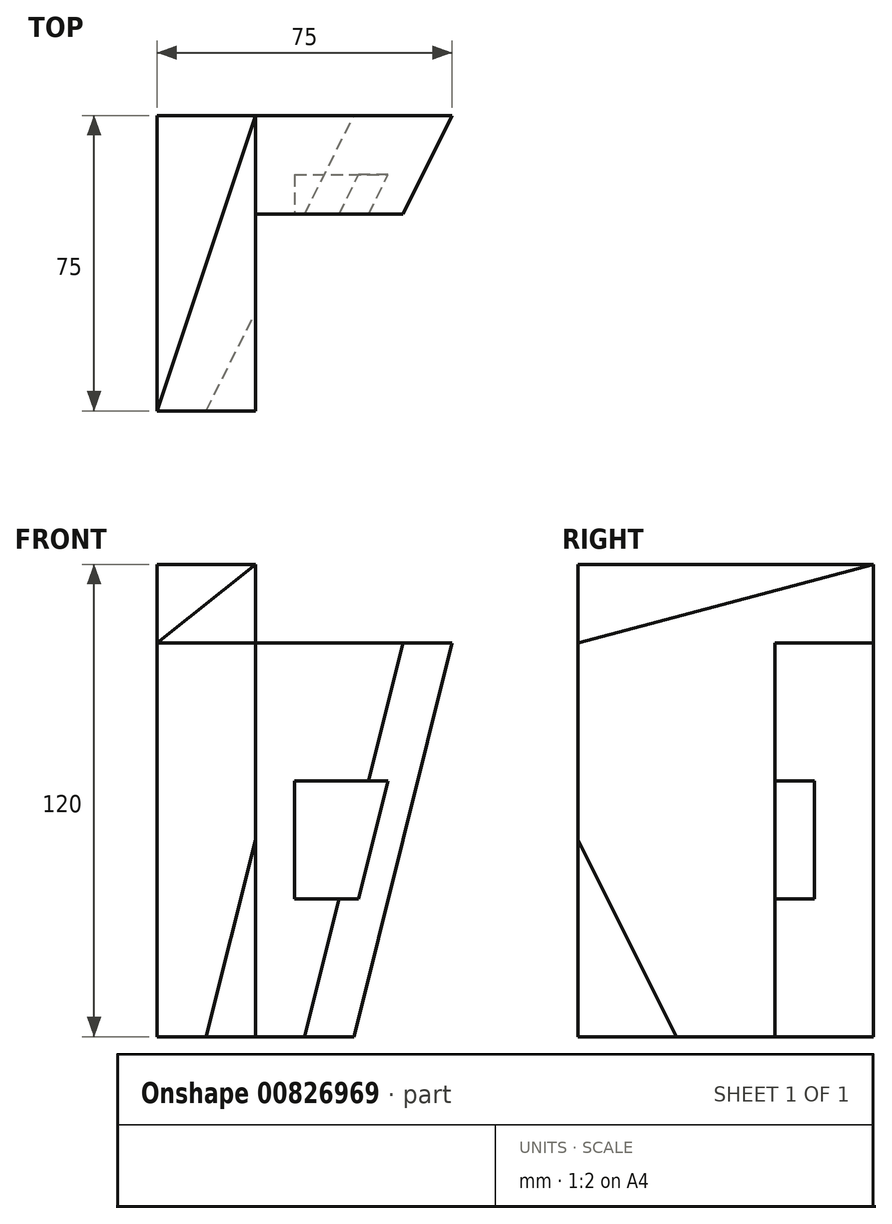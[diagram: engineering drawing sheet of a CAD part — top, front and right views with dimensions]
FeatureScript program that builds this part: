
annotation { "Feature Type Name" : "Feature", "Feature Type Description" : "" }
export const myFeature = defineFeature(function(context is Context, id is Id, definition is map)
    precondition{}
    {
        {
            var Q0;
            Q0=qCreatedBy(makeId("Top.planeOp"),FACE);
            var sketch = newSketch(context, id + "F0", { "sketchPlane" : qUnion([Q0])});
            skLineSegment(sketch, "E0.bottom", {"start": v(0, 0) * mm, "end": v(25, 0) * mm});
            skLineSegment(sketch, "E0.top", {"start": v(0, 75) * mm, "end": v(25, 75) * mm});
            skLineSegment(sketch, "E0.left", {"start": v(0, 0) * mm, "end": v(0, 75) * mm});
            skLineSegment(sketch, "E0.right", {"start": v(25, 0) * mm, "end": v(25, 75) * mm});
            skSolve(sketch);
        }
        {
            var Q0;
            Q0=makeQuery(id+"F0.imprint","IMPRINT",FACE,{"disambiguationData":[TD([[makeQuery(id+"F0.imprint","IMPRINT",EDGE,{"derivedFrom":sQuery(id+"F0.wireOp",EDGE,"E0.bottom")}),1.0]])]});
            extrude(context, id + "F1", {"entities" : qUnion([Q0]), "depth" : 120 * mm, "offsetDistance" : 25 * mm});
        }
        {
            var Q0;
            Q0=qCreatedBy(makeId("Top.planeOp"),FACE);
            var sketch = newSketch(context, id + "F2", { "sketchPlane" : qUnion([Q0])});
            skLineSegment(sketch, "E1.bottom", {"start": v(25, 75) * mm, "end": v(50, 75) * mm});
            skLineSegment(sketch, "E1.top", {"start": v(25, 50) * mm, "end": v(37.5, 50) * mm});
            skLineSegment(sketch, "E1.left", {"start": v(25, 75) * mm, "end": v(25, 50) * mm});
            skLineSegment(sketch, "E2", {"start": v(37.5, 50) * mm, "end": v(50, 75) * mm});
            skPoint(sketch, "E1.right.end.orphan", {"position": v(50, 50) * mm});
            skSolve(sketch);
        }
        {
            var Q0;
            Q0=qCreatedBy(makeId("Top.planeOp"),FACE);
            cPlane(context, id + "F3", {"entities" : qUnion([Q0]), "cplaneType" : CPlaneType.OFFSET, "offset" : 100 * mm, "width" : 150 * mm, "height" : 150 * mm});
        }
        {
            var Q0;
            Q0=qCreatedBy(id+"F3.planeOp",FACE);
            var sketch = newSketch(context, id + "F4", { "sketchPlane" : qUnion([Q0])});
            skLineSegment(sketch, "E3", {"start": v(25, 75) * mm, "end": v(25, 50) * mm});
            skLineSegment(sketch, "E4", {"start": v(25, 50) * mm, "end": v(62.5, 50) * mm});
            skLineSegment(sketch, "E5", {"start": v(62.5, 50) * mm, "end": v(75, 75) * mm});
            skLineSegment(sketch, "E6", {"start": v(75, 75) * mm, "end": v(25, 75) * mm});
            skSolve(sketch);
        }
        {
            var Q1;
            Q1=makeQuery(id+"F2.imprint","IMPRINT",FACE,{"disambiguationData":[TD([[makeQuery(id+"F2.imprint","IMPRINT",EDGE,{"derivedFrom":sQuery(id+"F2.wireOp",EDGE,"E1.bottom")}),-1.0]])]});
            var Q2;
            Q2=makeQuery(id+"F4.imprint","IMPRINT",FACE,{"disambiguationData":[TD([[makeQuery(id+"F4.imprint","IMPRINT",EDGE,{"derivedFrom":sQuery(id+"F4.wireOp",EDGE,"E3")}),1.0]])]});
            loft(context, id + "F5", {"operationType" : NewBodyOperationType.ADD, "sheetProfilesArray" : [{ "sheetProfileEntities" : qUnion([Q1]) }, { "sheetProfileEntities" : qUnion([Q2]) }]});
        }
        {
            var Q0;
            Q0=makeQuery(id+"F1.opExtrude","SWEPT_FACE",FACE,{"disambiguationData":[OSD([sQuery(id+"F0.wireOp",EDGE,"E0.bottom")])]});
            var sketch = newSketch(context, id + "F6", { "sketchPlane" : qUnion([Q0])});
            skLineSegment(sketch, "E7", {"start": v(0, 120) * mm, "end": v(0, 100) * mm});
            skLineSegment(sketch, "E8", {"start": v(0, 100) * mm, "end": v(25, 100) * mm});
            skLineSegment(sketch, "E9", {"start": v(25, 100) * mm, "end": v(25, 120) * mm});
            skLineSegment(sketch, "E10", {"start": v(25, 120) * mm, "end": v(0, 120) * mm});
            skSolve(sketch);
        }
        {
            var Q0;
            Q0=makeQuery(id+"F1.opExtrude","CAP_FACE",FACE,{"disambiguationData":[OSD([sQuery(id+"F0.wireOp",EDGE,"E0.bottom"),sQuery(id+"F0.wireOp",EDGE,"E0.top"),sQuery(id+"F0.wireOp",EDGE,"E0.left"),sQuery(id+"F0.wireOp",EDGE,"E0.right")])],"isStart":false});
            var sketch = newSketch(context, id + "F7", { "sketchPlane" : qUnion([Q0])});
            skPoint(sketch, "E11", {"position": v(25, 75) * mm});
            skSolve(sketch);
        }
        {
            var Q1;
            Q1=makeQuery(id+"F6.imprint","IMPRINT",FACE,{"disambiguationData":[TD([[makeQuery(id+"F6.imprint","IMPRINT",EDGE,{"derivedFrom":sQuery(id+"F6.wireOp",EDGE,"E7")}),1.0]])]});
            var Q2;
            Q2=sQuery(id+"F7.wireOp",VERTEX,"E11");
            loft(context, id + "F8", {"operationType" : NewBodyOperationType.REMOVE, "sheetProfilesArray" : [{ "sheetProfileEntities" : qUnion([Q1]) }, { "sheetProfileEntities" : qUnion([Q2]) }]});
        }
        {
            var Q0;
            Q0=makeQuery(id+"F5.boolean.opBoolean","MERGE",FACE,{"derivedFrom":[makeQuery(id+"F1.opExtrude","CAP_FACE",FACE,{"disambiguationData":[OSD([sQuery(id+"F0.wireOp",EDGE,"E0.bottom"),sQuery(id+"F0.wireOp",EDGE,"E0.top"),sQuery(id+"F0.wireOp",EDGE,"E0.left"),sQuery(id+"F0.wireOp",EDGE,"E0.right")])],"isStart":true}),makeQuery(id+"F5.opLoft","CAP_FACE",FACE,{"disambiguationData":[OSD([makeQuery(id+"F2.imprint","IMPRINT",FACE,{"disambiguationData":[TD([[makeQuery(id+"F2.imprint","IMPRINT",EDGE,{"derivedFrom":sQuery(id+"F2.wireOp",EDGE,"E1.bottom")}),-1.0]])]})])],"isStart":true})]});
            var sketch = newSketch(context, id + "F9", { "sketchPlane" : qUnion([Q0])});
            skLineSegment(sketch, "E12", {"start": v(12.5, 0) * mm, "end": v(25, -25) * mm});
            skLineSegment(sketch, "E13", {"start": v(25, -25) * mm, "end": v(25, 0) * mm});
            skLineSegment(sketch, "E14", {"start": v(25, 0) * mm, "end": v(12.5, 0) * mm});
            skSolve(sketch);
        }
        {
            var Q0;
            Q0=makeQuery(id+"F1.opExtrude","SWEPT_FACE",FACE,{"disambiguationData":[OSD([sQuery(id+"F0.wireOp",EDGE,"E0.bottom")])]});
            var sketch = newSketch(context, id + "F10", { "sketchPlane" : qUnion([Q0])});
            skPoint(sketch, "E15", {"position": v(25, 50) * mm});
            skSolve(sketch);
        }
        {
            var Q1;
            Q1=makeQuery(id+"F9.imprint","IMPRINT",FACE,{"disambiguationData":[TD([[makeQuery(id+"F9.imprint","IMPRINT",EDGE,{"derivedFrom":sQuery(id+"F9.wireOp",EDGE,"E12")}),1.0]])]});
            var Q2;
            Q2=sQuery(id+"F10.wireOp",VERTEX,"E15");
            loft(context, id + "F11", {"operationType" : NewBodyOperationType.REMOVE, "sheetProfilesArray" : [{ "sheetProfileEntities" : qUnion([Q1]) }, { "sheetProfileEntities" : qUnion([Q2]) }]});
        }
        {
            var Q0;
            Q0=makeQuery(id+"F1.opExtrude","SWEPT_FACE",FACE,{"disambiguationData":[OSD([sQuery(id+"F0.wireOp",EDGE,"E0.bottom")])]});
            var sketch = newSketch(context, id + "F12", { "sketchPlane" : qUnion([Q0])});
            skLineSegment(sketch, "E16.bottom", {"start": v(35, 65) * mm, "end": v(70, 65) * mm});
            skLineSegment(sketch, "E16.top", {"start": v(35, 35) * mm, "end": v(70, 35) * mm});
            skLineSegment(sketch, "E16.left", {"start": v(35, 65) * mm, "end": v(35, 35) * mm});
            skLineSegment(sketch, "E16.right", {"start": v(70, 65) * mm, "end": v(70, 35) * mm});
            skSolve(sketch);
        }
        {
            var Q0;
            Q0=makeQuery(id+"F12.imprint","IMPRINT",FACE,{"disambiguationData":[TD([[makeQuery(id+"F12.imprint","IMPRINT",EDGE,{"derivedFrom":sQuery(id+"F12.wireOp",EDGE,"E16.bottom")}),-1.0]])]});
            extrude(context, id + "F13", {"entities" : qUnion([Q0]), "operationType" : NewBodyOperationType.REMOVE, "oppositeDirection" : true, "depth" : 60 * mm, "offsetDistance" : 25 * mm});
        }
    });
